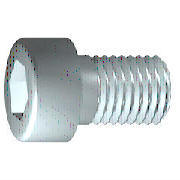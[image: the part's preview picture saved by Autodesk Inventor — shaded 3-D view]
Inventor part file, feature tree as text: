
AUTODESK INVENTOR PART (.ipt)
format: ipt  version: 2020 (Build 240168000, 168)  size: 194,560 bytes
history: native  units: mm (DEFAULTED — no unit token found)
features: sketch x2, extrude x1, plane x1, fillet x1
ambient origin geometry x7: Origin, YZ Plane, XY Plane, X Axis, Y Axis, Z Axis, Center Point
bodies: Solid1 (feature_tree), Body (feature_tree)
feature tree (5):
  extrude  "Slot"  Depth=3.5mm
  plane  "Work Plane1"
  fillet  "Fillet2"  Radius=3.5mm
  sketch  "Sketch1"  dims[d1=17.6mm d2=0.49086mm d3=3.5mm]
  sketch  "Sketch2"  dims[d4=2.7mm d5=60.0deg d6=5.0mm d7=5.0mm d8=3.464102mm d9=8.5mm d10=90.0deg d11=10.0mm d12=0.0mm d13=17.6mm d14=0.0mm d15=0.49076mm d16=0.49076mm d17=0.5mm d19=0.0mm d26=20.0mm d27=45.0deg d28=0.0mm d29=0.0mm d30=0.1mm]
